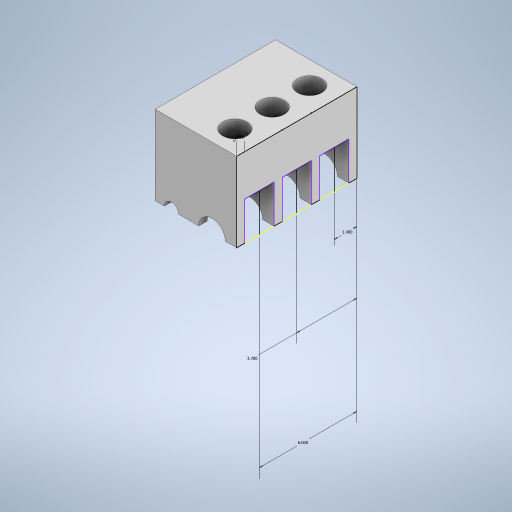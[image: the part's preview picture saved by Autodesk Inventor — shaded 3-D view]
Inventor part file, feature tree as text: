
AUTODESK INVENTOR PART (.ipt)
format: ipt  version: 2023 (Build 270158000, 158)  size: 342,016 bytes
history: native  units: in
note: dims shown in document units (in); Inventor stores cm internally (conversion verified against a paired STEP export)
features: extrude x4, sketch x3
ambient origin geometry x8: Origin, YZ Plane, XZ Plane, XY Plane, X Axis, Y Axis, Z Axis, Center Point
bodies: Solid1 (feature_tree)
feature tree (7):
  extrude  "Extrusion1"  Depth=4.878in
  sketch  "Sketch2"  dims[d2=1.625in d3=7.4in d4=0.0in]
  extrude  "Extrusion2"  Depth=7.4in TaperAngle=0.0deg
  extrude  "Extrusion3"  Depth=1.5in
  extrude  "Extrusion4"  Depth=1.5in
  sketch  "Sketch1"  dims[d0=5.0in d1=4.878in]
  sketch  "Sketch4"  dims[d5=1.5in d6=1.4in d7=1.5in d8=1.5in d9=1.5in d10=1.4in d11=1.5in d13=2.3in d14=1.5in d15=1.4in d16=3.7in d17=6.0in d18=0.5in d20=2.528in d21=7.4in d22=0.0in d23=7.4in d24=0.0in d25=1.5in d26=0.866in d27=1.5in d28=0.0in d29=0.0in d30=0.0in d31=0.0in d32=0.0in]
